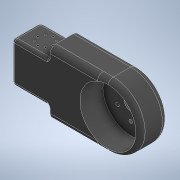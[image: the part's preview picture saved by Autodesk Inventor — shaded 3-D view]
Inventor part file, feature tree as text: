
AUTODESK INVENTOR PART (.ipt)
format: ipt  version: 2021 (Build 250183000, 183)  size: 282,624 bytes
history: native  units: mm
features: sketch x5, extrude x3, hole x3, fillet x2, pattern_circular x1
ambient origin geometry x8: Origin, YZ Plane, XZ Plane, XY Plane, X Axis, Y Axis, Z Axis, Center Point
bodies: Body1 (feature_tree)
feature tree (14):
  sketch  "Boceto1"  dims[d1=66.0mm d38=30.0mm d39=0.0mm]
  extrude  "Extrusión4"  Depth=30.0mm TaperAngle=0.0deg
  extrude  "Extrusión5"  Depth=6.0mm
  hole  "Agujero2"  [1 undecoded]
  pattern_circular  "Patrón circular2"  Count=6 Angle=360.0deg
  fillet  "Empalme5"  Radius=60.0mm
  sketch  "Boceto19"  dims[d73=16.0mm d74=3.0mm]
  sketch  "Boceto20"  dims[d75=3.688101mm d76=9.0mm d77=4.0mm d78=2.0mm d79=90.0deg d80=13.0mm d81=0.0mm d82=60.0mm d83=360.0deg d137=60.0mm]
  hole  "Agujero11"  [1 undecoded]
  hole  "Agujero12"  [1 undecoded]
  fillet  "Empalme7"  Radius=15.0mm
  extrude  "Extrusión22"  Depth=3.0mm
  sketch  "Boceto3"  dims[d40=6.0mm d41=0.0mm d72=40.0mm]
  sketch  "Boceto21"  dims[d149=6.0mm d389=21.0mm d390=21.0mm d444=15.0mm d445=8.2mm d446=20.0mm d447=8.0mm d448=2.1mm d449=80.0mm d451=360.0deg d453=15.0mm d454=8.2mm d455=8.0mm d456=2.1mm d457=80.0mm d459=360.0deg d461=2.013mm d462=5.0mm d463=5.0mm d464=4.0mm d465=90.0deg d466=6.5mm d467=0.0mm d468=2.013mm d469=5.0mm d470=5.0mm d471=4.0mm d472=90.0deg d473=6.5mm d474=0.0mm d475=3.0mm d476=13.736mm d477=30.0mm d478=0.0mm d53=0.5mm d54=0.872665mm d55=0.5mm d56=0.872665mm]
note: 3 required parameter values undecoded (feature->parameter linkage not recoverable at this tier; creation-order binding heuristic only, values carry confidence <= 0.55)
